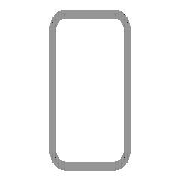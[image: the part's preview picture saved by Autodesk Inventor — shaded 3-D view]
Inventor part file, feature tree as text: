
AUTODESK INVENTOR PART (.ipt)
format: ipt  version: 2025 (Build 290162010, 162A)  size: 133,632 bytes
history: native  units: mm (DEFAULTED — no unit token found)
features: other x4, sketch x1, plane x1
ambient origin geometry x8: Origin, YZ Plane, XZ Plane, XY Plane, X Axis, Y Axis, Z Axis, Center Point
bodies: Solid1 (feature_tree), Body (feature_tree)
feature tree (6):
  parser-record x1  (decoder bookkeeping rows leaked as tree rows — omitted from the tree; the rows remain in map.json)
  other  "Driven Length"
  other  "Start Plane"
  other  "End Plane"
  sketch  "Sketch3"  dims[d3=347.0mm d4=0.0mm d7=6.0mm d9=40.0mm d11=60.0mm d12=3.0mm d13=40.0mm d14=387.0mm d15=20.0mm d16=30.0mm d17=90.0deg d18=347.0mm]
  plane  "Work Plane3"
